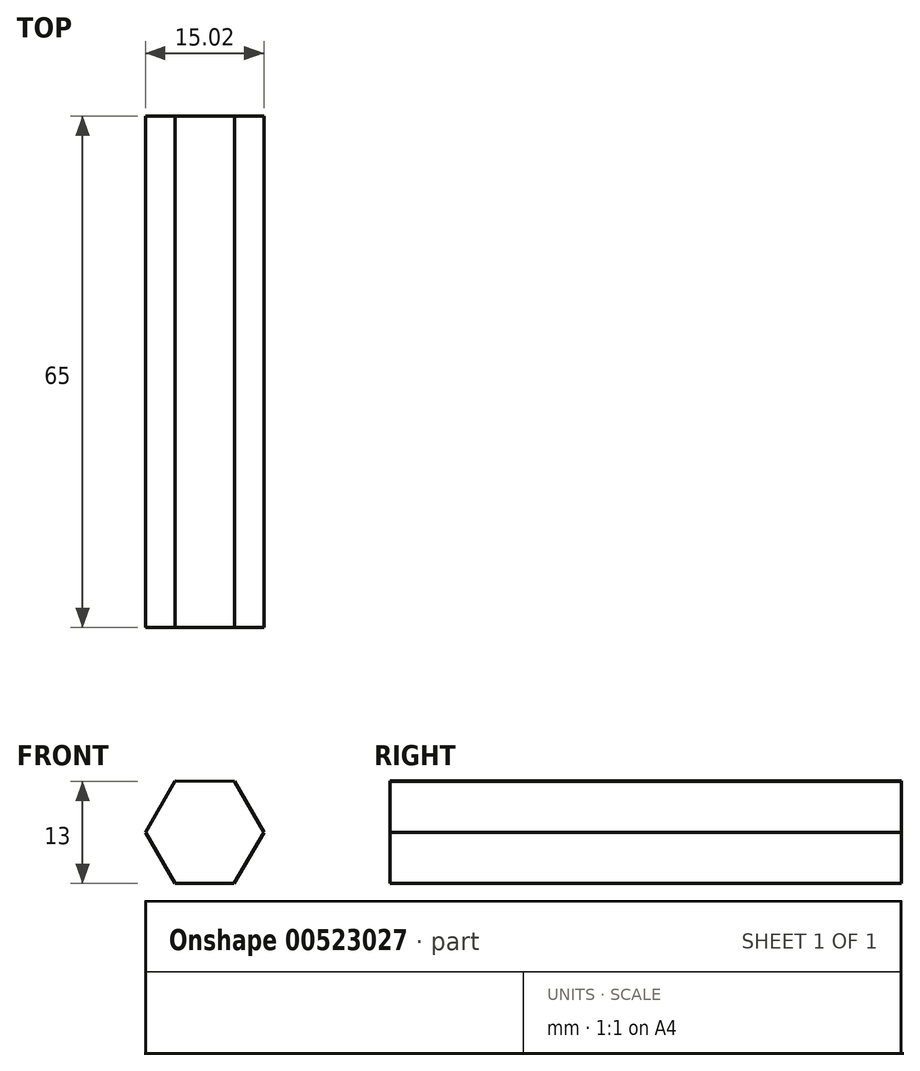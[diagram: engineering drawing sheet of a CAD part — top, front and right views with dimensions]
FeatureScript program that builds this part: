
annotation { "Feature Type Name" : "Feature", "Feature Type Description" : "" }
export const myFeature = defineFeature(function(context is Context, id is Id, definition is map)
    precondition{}
    {
        {
            var Q0;
            Q0=qCreatedBy(makeId("Front.planeOp"),FACE);
            var sketch = newSketch(context, id + "F0", { "sketchPlane" : qUnion([Q0])});
            skCircle(sketch, "E0.cCircle", {"center": v(0, 0) * mm, "radius": 6.5 * mm, "construction": true});
            skLineSegment(sketch, "E0.0", {"start": v(7.5, 0) * mm, "end": v(3.75, -6.5) * mm});
            skLineSegment(sketch, "E0.1", {"start": v(3.75, -6.5) * mm, "end": v(-3.76, -6.5) * mm});
            skLineSegment(sketch, "E0.2", {"start": v(-3.76, -6.5) * mm, "end": v(-7.5, 0) * mm});
            skLineSegment(sketch, "E0.3", {"start": v(-7.5, 0) * mm, "end": v(-3.75, 6.5) * mm});
            skLineSegment(sketch, "E0.4", {"start": v(-3.75, 6.5) * mm, "end": v(3.76, 6.5) * mm});
            skLineSegment(sketch, "E0.5", {"start": v(3.76, 6.5) * mm, "end": v(7.5, 0) * mm});
            skPoint(sketch, "E0.0.midPoint", {"position": v(5.63, -3.25) * mm});
            skSolve(sketch);
        }
        {
            var Q0;
            Q0 = qSketchRegion(id + "F0", true);
            extrude(context, id + "F1", {"entities" : qUnion([Q0]), "endBound" : BoundingType.SYMMETRIC, "depth" : 65 * mm, "offsetDistance" : 25 * mm});
        }
    });
